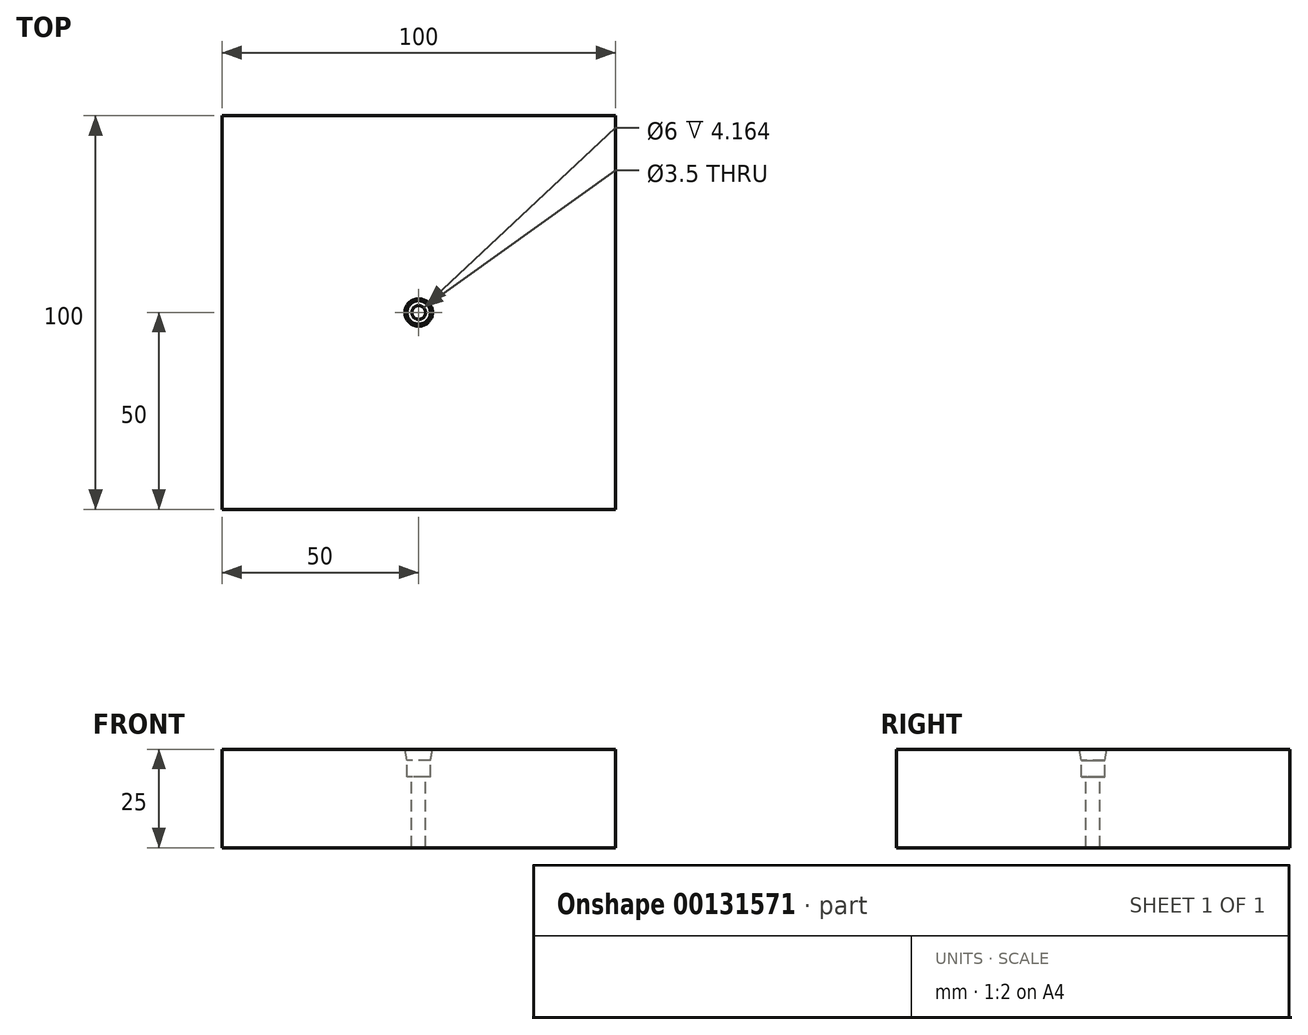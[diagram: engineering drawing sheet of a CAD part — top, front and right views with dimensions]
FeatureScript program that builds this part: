
annotation { "Feature Type Name" : "Feature", "Feature Type Description" : "" }
export const myFeature = defineFeature(function(context is Context, id is Id, definition is map)
    precondition{}
    {
        {
            var Q0;
            Q0=qCreatedBy(makeId("Top.planeOp"),FACE);
            var sketch = newSketch(context, id + "F0", { "sketchPlane" : qUnion([Q0])});
            skLineSegment(sketch, "E0.bottom", {"start": v(50, 50) * mm, "end": v(-50, 50) * mm});
            skLineSegment(sketch, "E0.top", {"start": v(50, -50) * mm, "end": v(-50, -50) * mm});
            skLineSegment(sketch, "E0.left", {"start": v(50, 50) * mm, "end": v(50, -50) * mm});
            skLineSegment(sketch, "E0.right", {"start": v(-50, 50) * mm, "end": v(-50, -50) * mm});
            skPoint(sketch, "E0.middle", {"position": v(0, 0) * mm});
            skSolve(sketch);
        }
        {
            var Q0;
            Q0=makeQuery(id+"F0.imprint","IMPRINT",FACE,{"disambiguationData":[TD([[makeQuery(id+"F0.imprint","IMPRINT",EDGE,{"derivedFrom":sQuery(id+"F0.wireOp",EDGE,"E0.bottom")}),1.0]])]});
            extrude(context, id + "F1", {"entities" : qUnion([Q0]), "depth" : 25 * mm});
        }
        {
            var Q0;
            Q0=makeQuery(id+"F1.opExtrude","CAP_FACE",FACE,{"disambiguationData":[OSD([sQuery(id+"F0.wireOp",EDGE,"E0.bottom"),sQuery(id+"F0.wireOp",EDGE,"E0.top"),sQuery(id+"F0.wireOp",EDGE,"E0.left"),sQuery(id+"F0.wireOp",EDGE,"E0.right")])],"isStart":false});
            var sketch = newSketch(context, id + "F2", { "sketchPlane" : qUnion([Q0])});
            skCircle(sketch, "E1", {"center": v(0, 0) * mm, "radius": 3 * mm});
            skSolve(sketch);
        }
        {
            var Q0;
            Q0=makeQuery(id+"F2.imprint","IMPRINT",FACE,{"disambiguationData":[TD([[makeQuery(id+"F2.imprint","IMPRINT",EDGE,{"derivedFrom":sQuery(id+"F2.wireOp",EDGE,"E1")}),1.0]])]});
            extrude(context, id + "F3", {"entities" : qUnion([Q0]), "operationType" : NewBodyOperationType.REMOVE, "oppositeDirection" : true, "depth" : 7 * mm});
        }
        {
            var Q0;
            Q0=makeQuery(id+"F3.boolean.opBoolean","COPY",FACE,{"derivedFrom":makeQuery(id+"F3.opExtrude","CAP_FACE",FACE,{"disambiguationData":[OSD([sQuery(id+"F2.wireOp",EDGE,"E1")])],"isStart":false})});
            var sketch = newSketch(context, id + "F4", { "sketchPlane" : qUnion([Q0])});
            skCircle(sketch, "E2", {"center": v(0, 0) * mm, "radius": 1.75 * mm});
            skSolve(sketch);
        }
        {
            var Q0;
            Q0=makeQuery(id+"F4.imprint","IMPRINT",FACE,{"disambiguationData":[TD([[makeQuery(id+"F4.imprint","IMPRINT",EDGE,{"derivedFrom":sQuery(id+"F4.wireOp",EDGE,"E2")}),1.0]])]});
            extrude(context, id + "F5", {"entities" : qUnion([Q0]), "operationType" : NewBodyOperationType.REMOVE, "oppositeDirection" : true, "depth" : 25 * mm});
        }
        {
            var Q0;
            Q0=qCreatedBy(makeId("Right.planeOp"),FACE);
            var sketch = newSketch(context, id + "F6", { "sketchPlane" : qUnion([Q0])});
            skLineSegment(sketch, "E3", {"start": v(0, 25) * mm, "end": v(-3.5, 25) * mm});
            skLineSegment(sketch, "E4", {"start": v(-3.5, 25) * mm, "end": v(-2.27, 18) * mm});
            skLineSegment(sketch, "E5", {"start": v(-2.27, 18) * mm, "end": v(0, 18) * mm});
            skLineSegment(sketch, "E6", {"start": v(0, 18) * mm, "end": v(0, 25) * mm});
            skSolve(sketch);
        }
        {
            var Q0;
            Q0=makeQuery(id+"F6.imprint","IMPRINT",FACE,{"disambiguationData":[TD([[makeQuery(id+"F6.imprint","IMPRINT",EDGE,{"derivedFrom":sQuery(id+"F6.wireOp",EDGE,"E3")}),1.0]])]});
            var Q1;
            Q1=sQuery(id+"F6.wireOp",EDGE,"E6");
            revolve(context, id + "F7", {"operationType" : NewBodyOperationType.REMOVE, "entities" : qUnion([Q0]), "axis" : qUnion([Q1]), "revolveType" : RevolveType.FULL, "oppositeDirection" : true});
        }
    });
